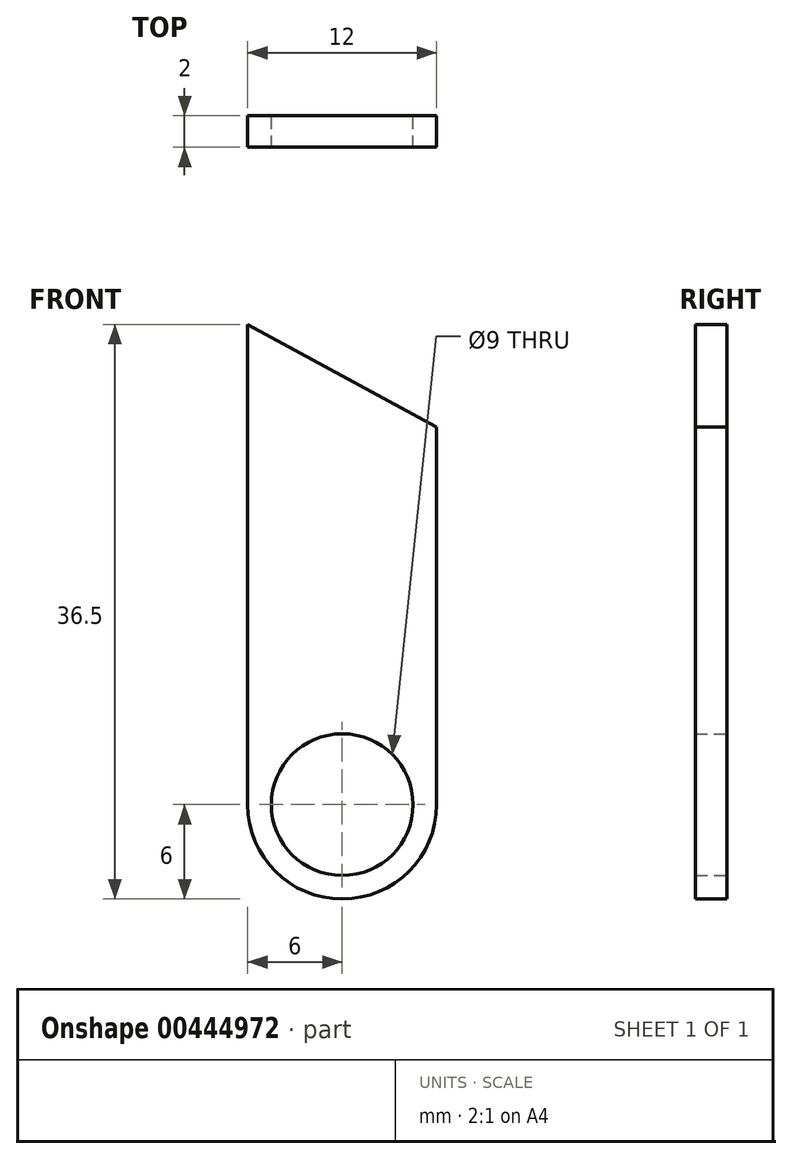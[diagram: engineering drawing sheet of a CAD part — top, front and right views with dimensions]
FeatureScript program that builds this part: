
annotation { "Feature Type Name" : "Feature", "Feature Type Description" : "" }
export const myFeature = defineFeature(function(context is Context, id is Id, definition is map)
    precondition{}
    {
        {
            var Q0;
            Q0=qCreatedBy(makeId("Front.planeOp"),FACE);
            var sketch = newSketch(context, id + "F0", { "sketchPlane" : qUnion([Q0])});
            skCircle(sketch, "E0", {"center": v(0, 0) * mm, "radius": 4.5 * mm});
            skArc(sketch, "E1", {"start": v(-6, 0) * mm, "mid": v(0, -6) * mm, "end": v(6, 0) * mm});
            skLineSegment(sketch, "E2", {"start": v(-6, 0) * mm, "end": v(-6, 30.5) * mm});
            skLineSegment(sketch, "E3", {"start": v(6, 0) * mm, "end": v(6, 23.98) * mm});
            skLineSegment(sketch, "E4", {"start": v(6, 23.98) * mm, "end": v(-6, 30.5) * mm});
            skSolve(sketch);
        }
        {
            var Q0;
            Q0 = qSketchRegion(id + "F0", true);
            extrude(context, id + "F1", {"entities" : qUnion([Q0]), "depth" : 2 * mm});
        }
    });
